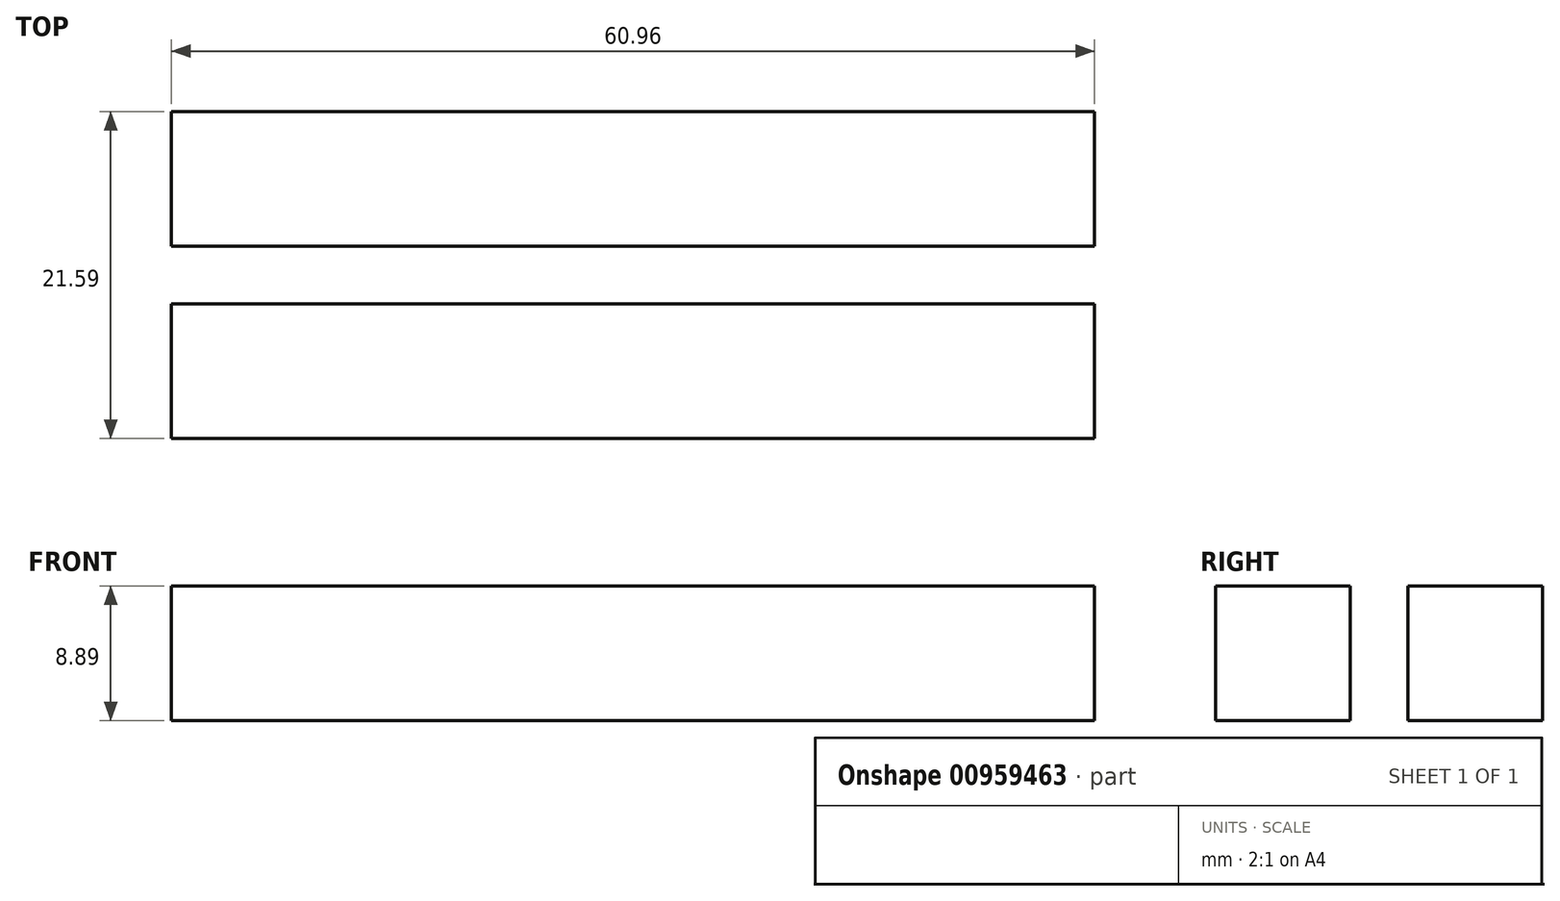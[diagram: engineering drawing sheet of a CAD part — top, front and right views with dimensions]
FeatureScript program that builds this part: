
annotation { "Feature Type Name" : "Feature", "Feature Type Description" : "" }
export const myFeature = defineFeature(function(context is Context, id is Id, definition is map)
    precondition{}
    {
        {
            var Q0;
            Q0=qCreatedBy(makeId("Top.planeOp"),FACE);
            var sketch = newSketch(context, id + "F0", { "sketchPlane" : qUnion([Q0])});
            skLineSegment(sketch, "E0.bottom", {"start": v(-60.96, -3.81) * mm, "end": v(0, -3.81) * mm});
            skLineSegment(sketch, "E0.top", {"start": v(-60.96, -12.7) * mm, "end": v(0, -12.7) * mm});
            skLineSegment(sketch, "E0.left", {"start": v(-60.96, -3.81) * mm, "end": v(-60.96, -12.7) * mm});
            skLineSegment(sketch, "E0.right", {"start": v(0, -3.81) * mm, "end": v(0, -12.7) * mm});
            skLineSegment(sketch, "E1.bottom", {"start": v(-60.96, 8.9) * mm, "end": v(0, 8.9) * mm});
            skLineSegment(sketch, "E1.top", {"start": v(-60.96, 0) * mm, "end": v(0, 0) * mm});
            skLineSegment(sketch, "E1.left", {"start": v(-60.96, 8.9) * mm, "end": v(-60.96, 0) * mm});
            skLineSegment(sketch, "E1.right", {"start": v(0, 8.9) * mm, "end": v(0, 0) * mm});
            skSolve(sketch);
        }
        {
            var Q0;
            Q0=makeQuery(id+"F0.imprint","IMPRINT",FACE,{"disambiguationData":[TD([[makeQuery(id+"F0.imprint","IMPRINT",EDGE,{"derivedFrom":sQuery(id+"F0.wireOp",EDGE,"E1.bottom")}),-1.0]])]});
            var Q1;
            Q1=makeQuery(id+"F0.imprint","IMPRINT",FACE,{"disambiguationData":[TD([[makeQuery(id+"F0.imprint","IMPRINT",EDGE,{"derivedFrom":sQuery(id+"F0.wireOp",EDGE,"E0.bottom")}),-1.0]])]});
            extrude(context, id + "F1", {"entities" : qUnion([Q0, Q1]), "depth" : 8.9 * mm, "offsetDistance" : 25.4 * mm});
        }
    });
